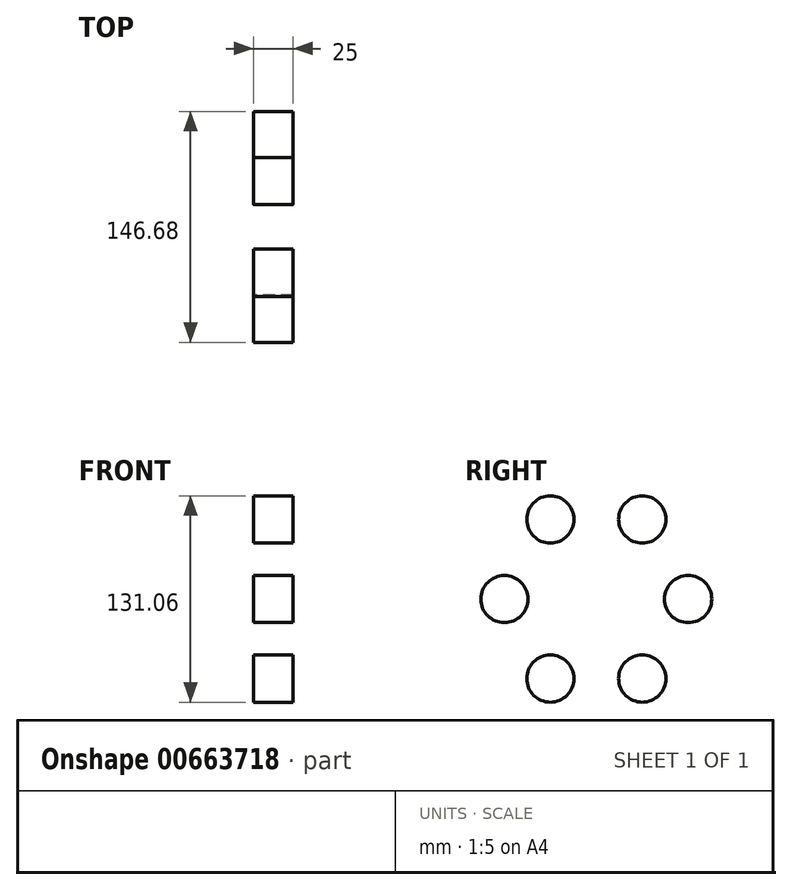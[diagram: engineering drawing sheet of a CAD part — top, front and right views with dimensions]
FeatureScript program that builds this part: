
annotation { "Feature Type Name" : "Feature", "Feature Type Description" : "" }
export const myFeature = defineFeature(function(context is Context, id is Id, definition is map)
    precondition{}
    {
        {
            var Q0;
            Q0=qCreatedBy(makeId("Right.planeOp"),FACE);
            var sketch = newSketch(context, id + "F0", { "sketchPlane" : qUnion([Q0])});
            skCircle(sketch, "E0", {"center": v(-58.34, 0) * mm, "radius": 15 * mm});
            skSolve(sketch);
        }
        {
            var Q0;
            Q0=qCreatedBy(makeId("Front.planeOp"),FACE);
            var sketch = newSketch(context, id + "F1", { "sketchPlane" : qUnion([Q0])});
            skLineSegment(sketch, "E1", {"start": v(0, 0) * mm, "end": v(38, 0) * mm});
            skSolve(sketch);
        }
        {
            var Q0;
            Q0 = qSketchRegion(id + "F0", true);
            extrude(context, id + "F2", {"entities" : qUnion([Q0]), "depth" : 25 * mm, "offsetDistance" : 25 * mm});
        }
        {
            var Q0;
            Q0=makeQuery(id+"F2.opExtrude","SWEPT_BODY",BODY,{"disambiguationData":[OSD([sQuery(id+"F0.wireOp",EDGE,"E0")])]});
            var Q1;
            Q1=sQuery(id+"F1.wireOp",EDGE,"E1");
            circularPattern(context, id + "F3", {"entities" : qUnion([Q0]), "axis" : qUnion([Q1]), "angle" : 360 * degree, "instanceCount" : 6, "equalSpace" : true});
        }
    });
